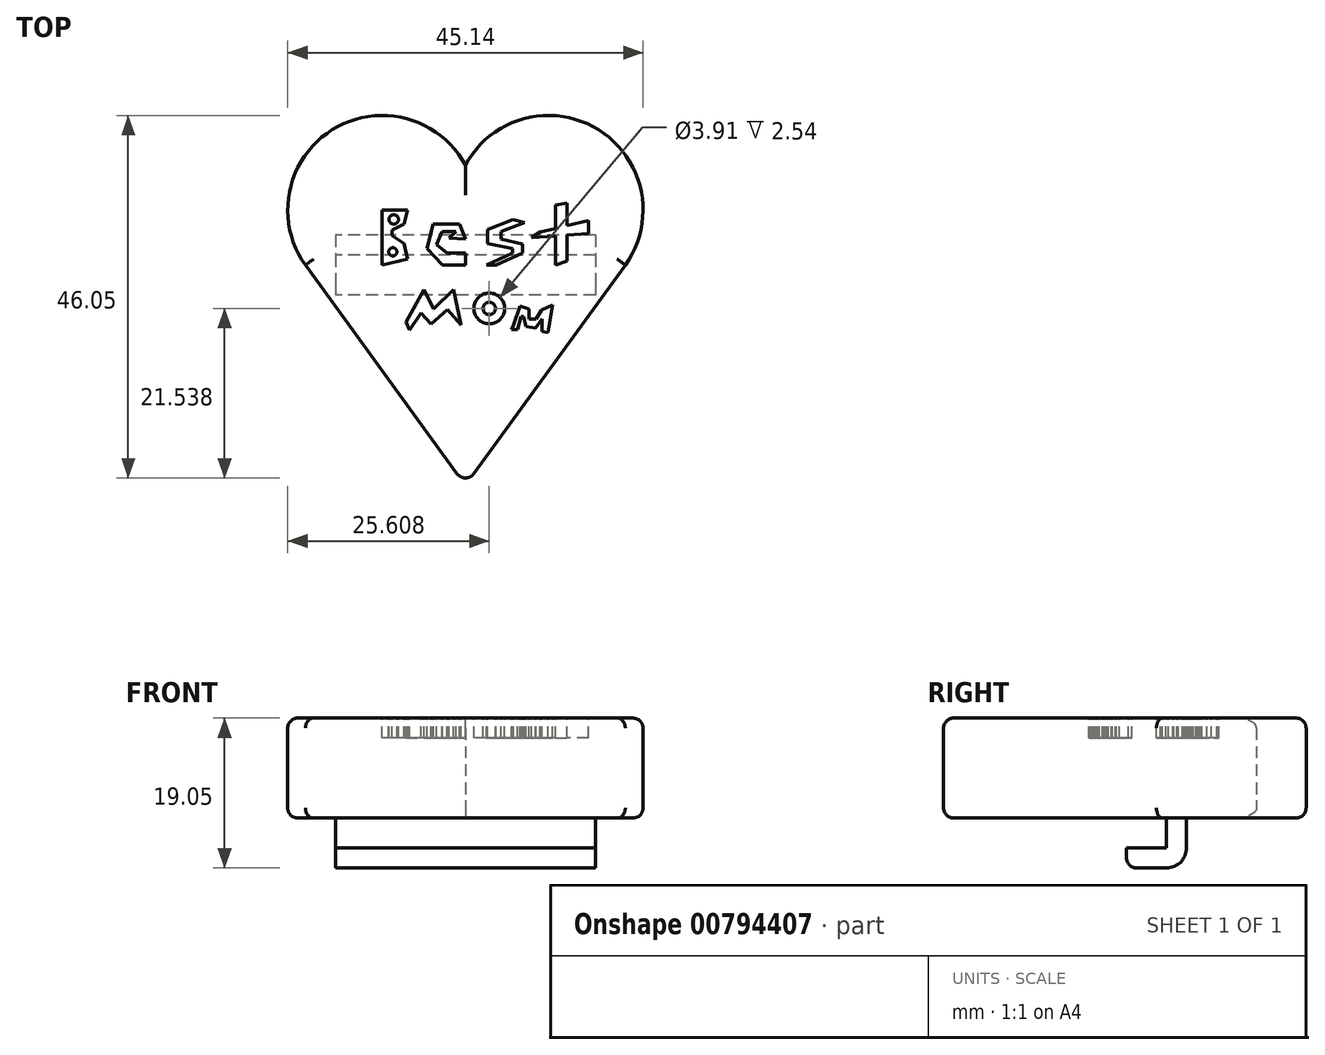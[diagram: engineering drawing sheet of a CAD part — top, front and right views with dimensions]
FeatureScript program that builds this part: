
annotation { "Feature Type Name" : "Feature", "Feature Type Description" : "" }
export const myFeature = defineFeature(function(context is Context, id is Id, definition is map)
    precondition{}
    {
        {
            var Q0;
            Q0=qCreatedBy(makeId("Top.planeOp"),FACE);
            var sketch = newSketch(context, id + "F0", { "sketchPlane" : qUnion([Q0])});
            skLineSegment(sketch, "E0", {"start": v(0, 12.7) * mm, "end": v(0, -27.94) * mm});
            skLineSegment(sketch, "E1", {"start": v(0, 12.7) * mm, "end": v(0, 0) * mm});
            skLineSegment(sketch, "E2", {"start": v(0, 0) * mm, "end": v(0, -27.94) * mm});
            skLineSegment(sketch, "E3", {"start": v(0, 0) * mm, "end": v(-20.32, 0) * mm});
            skLineSegment(sketch, "E4", {"start": v(0, 0) * mm, "end": v(20.32, 0) * mm});
            skLineSegment(sketch, "E5", {"start": v(0, 0) * mm, "end": v(-13.11, 18.73) * mm});
            skLineSegment(sketch, "E6", {"start": v(0, 0) * mm, "end": v(13.11, 18.73) * mm});
            skArc(sketch, "E7", {"start": v(0, 12.7) * mm, "mid": v(-16.93, 17.17) * mm, "end": v(-20.32, 0) * mm});
            skArc(sketch, "E8", {"start": v(20.32, 0) * mm, "mid": v(16.93, 17.17) * mm, "end": v(0, 12.7) * mm});
            skLineSegment(sketch, "E9", {"start": v(-20.32, 0) * mm, "end": v(0, -27.94) * mm});
            skLineSegment(sketch, "E10", {"start": v(0, -27.94) * mm, "end": v(20.32, 0) * mm});
            skSolve(sketch);
        }
        {
            var Q0;
            {var subQ0=sQuery(id+"F0.wireOp",EDGE,"E3");Q0=makeQuery(id+"F0.imprint","IMPRINT",FACE,{"disambiguationData":[TD([[makeQuery(id+"F0.imprint","IMPRINT",EDGE,{"derivedFrom":subQ0}),1.0]])]});}
            var Q1;
            {var subQ0=sQuery(id+"F0.wireOp",EDGE,"E3");Q1=makeQuery(id+"F0.imprint","IMPRINT",FACE,{"disambiguationData":[TD([[makeQuery(id+"F0.imprint","IMPRINT",EDGE,{"derivedFrom":subQ0}),-1.0]])]});}
            var Q2;
            {var subQ0=sQuery(id+"F0.wireOp",EDGE,"E5");Q2=makeQuery(id+"F0.imprint","IMPRINT",FACE,{"disambiguationData":[TD([[makeQuery(id+"F0.imprint","IMPRINT",EDGE,{"derivedFrom":subQ0}),-1.0]])]});}
            var Q3;
            {var subQ0=sQuery(id+"F0.wireOp",EDGE,"E6");Q3=makeQuery(id+"F0.imprint","IMPRINT",FACE,{"disambiguationData":[TD([[makeQuery(id+"F0.imprint","IMPRINT",EDGE,{"derivedFrom":subQ0}),1.0]])]});}
            var Q4;
            {var subQ0=sQuery(id+"F0.wireOp",EDGE,"E4");Q4=makeQuery(id+"F0.imprint","IMPRINT",FACE,{"disambiguationData":[TD([[makeQuery(id+"F0.imprint","IMPRINT",EDGE,{"derivedFrom":subQ0}),1.0]])]});}
            var Q5;
            {var subQ0=sQuery(id+"F0.wireOp",EDGE,"E4");Q5=makeQuery(id+"F0.imprint","IMPRINT",FACE,{"disambiguationData":[TD([[makeQuery(id+"F0.imprint","IMPRINT",EDGE,{"derivedFrom":subQ0}),-1.0]])]});}
            extrude(context, id + "F1", {"entities" : qUnion([Q0, Q1, Q2, Q3, Q4, Q5]), "depth" : 12.7 * mm, "offsetDistance" : 25.4 * mm});
        }
        {
            var Q0;
            Q0=makeQuery(id+"F1.opExtrude","SWEPT_EDGE",EDGE,{"disambiguationData":[OSD([sQuery(id+"F0.wireOp",EDGE,"E0"),sQuery(id+"F0.wireOp",EDGE,"E9"),sQuery(id+"F0.wireOp",EDGE,"E10")])]});
            fillet(context, id + "F2", {"entities" : qUnion([Q0]), "radius" : 1.27 * mm, "tangentPropagation" : true, "allowEdgeOverflow" : false});
        }
        {
            var Q0;
            Q0=makeQuery(id+"F1.opExtrude","CAP_FACE",FACE,{"disambiguationData":[OSD([sQuery(id+"F0.wireOp",EDGE,"E7"),sQuery(id+"F0.wireOp",EDGE,"E8"),sQuery(id+"F0.wireOp",EDGE,"E9"),sQuery(id+"F0.wireOp",EDGE,"E10")])],"isStart":true});
            var sketch = newSketch(context, id + "F3", { "sketchPlane" : qUnion([Q0])});
            skLineSegment(sketch, "E11.bottom", {"start": v(16.5, -3.81) * mm, "end": v(-16.5, -3.81) * mm});
            skLineSegment(sketch, "E11.top", {"start": v(16.5, 3.81) * mm, "end": v(-16.5, 3.81) * mm});
            skLineSegment(sketch, "E11.left", {"start": v(16.5, -3.81) * mm, "end": v(16.5, 3.81) * mm});
            skLineSegment(sketch, "E11.right", {"start": v(-16.5, -3.81) * mm, "end": v(-16.5, 3.81) * mm});
            skPoint(sketch, "E11.middle", {"position": v(0, 0) * mm});
            skSolve(sketch);
        }
        {
            var Q0;
            Q0=makeQuery(id+"F3.imprint","IMPRINT",FACE,{"disambiguationData":[TD([[makeQuery(id+"F3.imprint","IMPRINT",EDGE,{"derivedFrom":sQuery(id+"F3.wireOp",EDGE,"E11.bottom")}),-1.0]])]});
            extrude(context, id + "F4", {"entities" : qUnion([Q0]), "operationType" : NewBodyOperationType.ADD, "depth" : 6.35 * mm, "offsetDistance" : 25.4 * mm});
        }
        {
            var Q0;
            Q0=makeQuery(id+"F4.opExtrude","SWEPT_FACE",FACE,{"disambiguationData":[OSD([sQuery(id+"F3.wireOp",EDGE,"E11.top")])]});
            var sketch = newSketch(context, id + "F5", { "sketchPlane" : qUnion([Q0])});
            skLineSegment(sketch, "E12", {"start": v(0, -6.35) * mm, "end": v(0, -3.81) * mm});
            skLineSegment(sketch, "E13.0", {"start": v(16.5, -6.35) * mm, "end": v(16.5, 0) * mm});
            skLineSegment(sketch, "E14.0", {"start": v(-16.5, -6.35) * mm, "end": v(-16.5, 0) * mm});
            skLineSegment(sketch, "E15", {"start": v(0, -3.81) * mm, "end": v(16.5, -3.81) * mm});
            skLineSegment(sketch, "E16", {"start": v(16.5, -3.81) * mm, "end": v(-16.5, -3.81) * mm});
            skLineSegment(sketch, "E17.0", {"start": v(16.5, 0) * mm, "end": v(-16.5, 0) * mm});
            skSolve(sketch);
        }
        {
            var Q0;
            {var subQ6=sQuery(id+"F5.wireOp",EDGE,"E17.0");Q0=makeQuery(id+"F5.imprint","IMPRINT",FACE,{"disambiguationData":[TD([[makeQuery(id+"F5.imprint","IMPRINT",EDGE,{"derivedFrom":subQ6}),1.0]])]});}
            extrude(context, id + "F6", {"entities" : qUnion([Q0]), "operationType" : NewBodyOperationType.REMOVE, "oppositeDirection" : true, "depth" : 5.08 * mm, "offsetDistance" : 25.4 * mm});
        }
        {
            var Q0;
            Q0=makeQuery(id+"F4.opExtrude","CAP_EDGE",EDGE,{"disambiguationData":[OSD([sQuery(id+"F3.wireOp",EDGE,"E11.bottom")])],"isStart":false});
            fillet(context, id + "F7", {"entities" : qUnion([Q0]), "radius" : 2.54 * mm, "tangentPropagation" : true, "allowEdgeOverflow" : false});
        }
        {
            var Q0;
            Q0=makeQuery(id+"F6.boolean.opBoolean","COPY",EDGE,{"derivedFrom":makeQuery(id+"F6.opExtrude","CAP_EDGE",EDGE,{"disambiguationData":[OSD([sQuery(id+"F5.wireOp",EDGE,"E16")])],"isStart":true})});
            var Q1;
            Q1=makeQuery(id+"F4.opExtrude","CAP_EDGE",EDGE,{"disambiguationData":[OSD([sQuery(id+"F3.wireOp",EDGE,"E11.top")])],"isStart":false});
            var Q2;
            Q2=makeQuery(id+"F1.opExtrude","CAP_EDGE",EDGE,{"disambiguationData":[OSD([sQuery(id+"F0.wireOp",EDGE,"E9")])],"isStart":false});
            var Q3;
            Q3=makeQuery(id+"F1.opExtrude","CAP_EDGE",EDGE,{"disambiguationData":[OSD([sQuery(id+"F0.wireOp",EDGE,"E10")])],"isStart":true});
            fillet(context, id + "F8", {"entities" : qUnion([Q0, Q1, Q2, Q3]), "radius" : 1.27 * mm, "tangentPropagation" : true, "allowEdgeOverflow" : false});
        }
        {
            var Q0;
            Q0=makeQuery(id+"F1.opExtrude","CAP_EDGE",EDGE,{"disambiguationData":[OSD([sQuery(id+"F0.wireOp",EDGE,"E7")])],"isStart":false});
            var Q1;
            Q1=makeQuery(id+"F1.opExtrude","CAP_EDGE",EDGE,{"disambiguationData":[OSD([sQuery(id+"F0.wireOp",EDGE,"E8")])],"isStart":false});
            fillet(context, id + "F9", {"entities" : qUnion([Q0, Q1]), "radius" : 1.27 * mm, "tangentPropagation" : true, "allowEdgeOverflow" : false});
        }
        {
            var Q0;
            Q0=makeQuery(id+"F1.opExtrude","CAP_FACE",FACE,{"disambiguationData":[OSD([sQuery(id+"F0.wireOp",EDGE,"E7"),sQuery(id+"F0.wireOp",EDGE,"E8"),sQuery(id+"F0.wireOp",EDGE,"E9"),sQuery(id+"F0.wireOp",EDGE,"E10")])],"isStart":false});
            var sketch = newSketch(context, id + "F10", { "sketchPlane" : qUnion([Q0])});
            skLineSegment(sketch, "E18", {"start": v(-10.56, 7) * mm, "end": v(-10.56, 0) * mm});
            skLineSegment(sketch, "E19", {"start": v(-10.56, 0) * mm, "end": v(-7.33, 0.73) * mm});
            skLineSegment(sketch, "E20", {"start": v(-7.33, 0.73) * mm, "end": v(-7.8, 2.74) * mm});
            skLineSegment(sketch, "E21", {"start": v(-7.8, 2.74) * mm, "end": v(-9.3, 3.73) * mm});
            skLineSegment(sketch, "E22", {"start": v(-9.3, 3.73) * mm, "end": v(-9.3, 4.41) * mm});
            skLineSegment(sketch, "E23", {"start": v(-9.3, 4.41) * mm, "end": v(-7.8, 5.18) * mm});
            skLineSegment(sketch, "E24", {"start": v(-7.8, 5.18) * mm, "end": v(-7.33, 7) * mm});
            skLineSegment(sketch, "E25", {"start": v(-7.33, 7) * mm, "end": v(-10.56, 7) * mm});
            skLineSegment(sketch, "E26", {"start": v(0, 3.32) * mm, "end": v(-0.74, 5.2) * mm});
            skLineSegment(sketch, "E27", {"start": v(-0.74, 5.2) * mm, "end": v(-4.12, 5.2) * mm});
            skLineSegment(sketch, "E28", {"start": v(-4.12, 5.2) * mm, "end": v(-4.84, 2.1) * mm});
            skLineSegment(sketch, "E29", {"start": v(-4.84, 2.1) * mm, "end": v(-2.9, 0) * mm});
            skLineSegment(sketch, "E30", {"start": v(-2.9, 0) * mm, "end": v(0, 0) * mm});
            skLineSegment(sketch, "E31", {"start": v(0, 0) * mm, "end": v(0, 1.5) * mm});
            skLineSegment(sketch, "E32", {"start": v(0, 1.5) * mm, "end": v(-2.35, 1.5) * mm});
            skLineSegment(sketch, "E33", {"start": v(-2.35, 1.5) * mm, "end": v(-3.67, 2.61) * mm});
            skLineSegment(sketch, "E34", {"start": v(-3.67, 2.61) * mm, "end": v(-2.99, 4.24) * mm});
            skLineSegment(sketch, "E35", {"start": v(-2.99, 4.24) * mm, "end": v(-1.2, 4.24) * mm});
            skLineSegment(sketch, "E36", {"start": v(-1.2, 4.24) * mm, "end": v(-2.1, 3.42) * mm});
            skPoint(sketch, "E36.endSnap0", {"position": v(-2.1, 4.24) * mm});
            skLineSegment(sketch, "E37", {"start": v(-2.1, 3.42) * mm, "end": v(0, 3.32) * mm});
            skLineSegment(sketch, "E38", {"start": v(6.07, 5.79) * mm, "end": v(2.84, 4.5) * mm});
            skLineSegment(sketch, "E39", {"start": v(2.84, 4.5) * mm, "end": v(2.84, 2.74) * mm});
            skLineSegment(sketch, "E40", {"start": v(2.84, 2.74) * mm, "end": v(6, 2.1) * mm});
            skLineSegment(sketch, "E41", {"start": v(6, 2.1) * mm, "end": v(6, 1.5) * mm});
            skLineSegment(sketch, "E42", {"start": v(6, 1.5) * mm, "end": v(2.66, 0) * mm});
            skLineSegment(sketch, "E43", {"start": v(2.66, 0) * mm, "end": v(3.9, 0) * mm});
            skLineSegment(sketch, "E44", {"start": v(3.9, 0) * mm, "end": v(7.28, 1.5) * mm});
            skLineSegment(sketch, "E45", {"start": v(7.28, 1.5) * mm, "end": v(7.28, 2.68) * mm});
            skLineSegment(sketch, "E46", {"start": v(7.28, 2.68) * mm, "end": v(4.55, 3.28) * mm});
            skLineSegment(sketch, "E47", {"start": v(4.55, 3.28) * mm, "end": v(4.55, 4.27) * mm});
            skLineSegment(sketch, "E48", {"start": v(4.55, 4.27) * mm, "end": v(7.54, 5.42) * mm});
            skLineSegment(sketch, "E49", {"start": v(7.54, 5.42) * mm, "end": v(6.07, 5.79) * mm});
            skLineSegment(sketch, "E50", {"start": v(11.43, 7.65) * mm, "end": v(11.43, 0) * mm});
            skLineSegment(sketch, "E51", {"start": v(11.43, 0) * mm, "end": v(12.88, 0.51) * mm});
            skLineSegment(sketch, "E52", {"start": v(12.88, 0.51) * mm, "end": v(12.88, 7.9) * mm});
            skLineSegment(sketch, "E53", {"start": v(12.88, 7.9) * mm, "end": v(11.43, 7.65) * mm});
            skLineSegment(sketch, "E54", {"start": v(9.5, 4.2) * mm, "end": v(15.67, 5.65) * mm});
            skPoint(sketch, "E54.startSnap0", {"position": v(12.88, 4.2) * mm});
            skLineSegment(sketch, "E55", {"start": v(15.67, 5.65) * mm, "end": v(15.67, 4.02) * mm});
            skLineSegment(sketch, "E56", {"start": v(15.67, 4.02) * mm, "end": v(8.4, 3.48) * mm});
            skLineSegment(sketch, "E57", {"start": v(8.4, 3.48) * mm, "end": v(9.5, 4.2) * mm});
            skLineSegment(sketch, "E58", {"start": v(-7.54, -7.24) * mm, "end": v(-5.24, -3.12) * mm});
            skLineSegment(sketch, "E59", {"start": v(-5.24, -3.12) * mm, "end": v(-4.03, -5.6) * mm});
            skLineSegment(sketch, "E60", {"start": v(-4.03, -5.6) * mm, "end": v(-1.5, -3.12) * mm});
            skLineSegment(sketch, "E61", {"start": v(-1.5, -3.12) * mm, "end": v(-0.52, -7.6) * mm});
            skLineSegment(sketch, "E62", {"start": v(-0.52, -7.6) * mm, "end": v(-2.28, -5.66) * mm});
            skLineSegment(sketch, "E63", {"start": v(-2.28, -5.66) * mm, "end": v(-4.33, -7.52) * mm});
            skLineSegment(sketch, "E64", {"start": v(-4.33, -7.52) * mm, "end": v(-5.62, -6.1) * mm});
            skLineSegment(sketch, "E65", {"start": v(-5.62, -6.1) * mm, "end": v(-7.12, -8.27) * mm});
            skLineSegment(sketch, "E66", {"start": v(-7.12, -8.27) * mm, "end": v(-7.54, -7.24) * mm});
            skCircle(sketch, "E67", {"center": v(3.04, -5.51) * mm, "radius": 1.96 * mm});
            skCircle(sketch, "E68", {"center": v(3.04, -5.51) * mm, "radius": 0.8 * mm});
            skLineSegment(sketch, "E69", {"start": v(6.1, -7.6) * mm, "end": v(6.96, -5.2) * mm});
            skLineSegment(sketch, "E70", {"start": v(6.96, -5.2) * mm, "end": v(8.07, -5.6) * mm});
            skLineSegment(sketch, "E71", {"start": v(8.07, -5.6) * mm, "end": v(8.07, -6.83) * mm});
            skLineSegment(sketch, "E72", {"start": v(8.07, -6.83) * mm, "end": v(9, -6.83) * mm});
            skLineSegment(sketch, "E73", {"start": v(9, -6.83) * mm, "end": v(9.7, -5.72) * mm});
            skLineSegment(sketch, "E74", {"start": v(9.7, -5.72) * mm, "end": v(11.08, -5.1) * mm});
            skLineSegment(sketch, "E75", {"start": v(11.08, -5.1) * mm, "end": v(10.52, -8.56) * mm});
            skLineSegment(sketch, "E76", {"start": v(10.52, -8.56) * mm, "end": v(9.73, -8.44) * mm});
            skLineSegment(sketch, "E77", {"start": v(9.73, -8.44) * mm, "end": v(9.73, -6.89) * mm});
            skLineSegment(sketch, "E78", {"start": v(9.73, -6.89) * mm, "end": v(8.94, -8) * mm});
            skLineSegment(sketch, "E79", {"start": v(8.94, -8) * mm, "end": v(7.73, -7.8) * mm});
            skLineSegment(sketch, "E80", {"start": v(7.73, -7.8) * mm, "end": v(7.4, -6.53) * mm});
            skLineSegment(sketch, "E81", {"start": v(7.4, -6.53) * mm, "end": v(7.1, -6.53) * mm});
            skLineSegment(sketch, "E82", {"start": v(7.1, -6.53) * mm, "end": v(6.6, -8.18) * mm});
            skLineSegment(sketch, "E83", {"start": v(6.6, -8.18) * mm, "end": v(5.84, -8.18) * mm});
            skLineSegment(sketch, "E84", {"start": v(5.84, -8.18) * mm, "end": v(6.1, -7.6) * mm});
            skCircle(sketch, "E85", {"center": v(-9.22, 1.68) * mm, "radius": 0.52 * mm});
            skCircle(sketch, "E86", {"center": v(-9.1, 5.8) * mm, "radius": 0.6 * mm});
            skSolve(sketch);
        }
        {
            var Q0;
            Q0=makeQuery(id+"F10.imprint","IMPRINT",FACE,{"disambiguationData":[TD([[makeQuery(id+"F10.imprint","IMPRINT",EDGE,{"derivedFrom":sQuery(id+"F10.wireOp",EDGE,"E18")}),1.0]])]});
            var Q1;
            Q1=makeQuery(id+"F10.imprint","IMPRINT",FACE,{"disambiguationData":[TD([[makeQuery(id+"F10.imprint","IMPRINT",EDGE,{"derivedFrom":sQuery(id+"F10.wireOp",EDGE,"E58")}),-1.0]])]});
            var Q2;
            Q2=makeQuery(id+"F10.imprint","IMPRINT",FACE,{"disambiguationData":[TD([[makeQuery(id+"F10.imprint","IMPRINT",EDGE,{"derivedFrom":sQuery(id+"F10.wireOp",EDGE,"E26")}),1.0]])]});
            var Q3;
            Q3=makeQuery(id+"F10.imprint","IMPRINT",FACE,{"disambiguationData":[TD([[makeQuery(id+"F10.imprint","IMPRINT",EDGE,{"derivedFrom":sQuery(id+"F10.wireOp",EDGE,"E38")}),1.0]])]});
            var Q4;
            {var subQ0=sQuery(id+"F10.wireOp",EDGE,"E51");Q4=makeQuery(id+"F10.imprint","IMPRINT",FACE,{"disambiguationData":[TD([[makeQuery(id+"F10.imprint","IMPRINT",EDGE,{"derivedFrom":subQ0}),1.0]])]});}
            var Q5;
            {var subQ5=sQuery(id+"F10.wireOp",EDGE,"E57");Q5=makeQuery(id+"F10.imprint","IMPRINT",FACE,{"disambiguationData":[TD([[makeQuery(id+"F10.imprint","IMPRINT",EDGE,{"derivedFrom":subQ5}),-1.0]])]});}
            var Q6;
            {var subQ0=sQuery(id+"F10.wireOp",EDGE,"E53");Q6=makeQuery(id+"F10.imprint","IMPRINT",FACE,{"disambiguationData":[TD([[makeQuery(id+"F10.imprint","IMPRINT",EDGE,{"derivedFrom":subQ0}),1.0]])]});}
            var Q7;
            {var subQ5=sQuery(id+"F10.wireOp",EDGE,"E55");Q7=makeQuery(id+"F10.imprint","IMPRINT",FACE,{"disambiguationData":[TD([[makeQuery(id+"F10.imprint","IMPRINT",EDGE,{"derivedFrom":subQ5}),-1.0]])]});}
            var Q8;
            {var subQ0=sQuery(id+"F10.wireOp",EDGE,"E54");var subQ1=sQuery(id+"F10.wireOp",EDGE,"E50");var subQ2=makeQuery(id+"F10.imprint","INTERSECT",VERTEX,{"derivedFrom":[subQ1,subQ0]});Q8=makeQuery(id+"F10.imprint","IMPRINT",FACE,{"disambiguationData":[TD([[makeQuery(id+"F10.imprint","IMPRINT",EDGE,{"disambiguationData":[TD([[subQ2,-1.0]])],"derivedFrom":subQ1}),1.0]])]});}
            var Q9;
            Q9=makeQuery(id+"F10.imprint","IMPRINT",FACE,{"disambiguationData":[TD([[makeQuery(id+"F10.imprint","IMPRINT",EDGE,{"derivedFrom":sQuery(id+"F10.wireOp",EDGE,"E69")}),-1.0]])]});
            var Q10;
            Q10=makeQuery(id+"F10.imprint","IMPRINT",FACE,{"disambiguationData":[TD([[makeQuery(id+"F10.imprint","IMPRINT",EDGE,{"derivedFrom":sQuery(id+"F10.wireOp",EDGE,"E67")}),1.0]])]});
            extrude(context, id + "F11", {"entities" : qUnion([Q0, Q1, Q2, Q3, Q4, Q5, Q6, Q7, Q8, Q9, Q10]), "operationType" : NewBodyOperationType.REMOVE, "oppositeDirection" : true, "depth" : 2.54 * mm, "offsetDistance" : 25.4 * mm});
        }
    });
